# Revit family: Screens-Teknion-JNSEEH_Felt_Elevated_Height_Adjustable_Mounted-R2018
name_source: partatom
category: Furniture
revit_build: Autodesk Revit 2018 (Build: 20190510_1515(x64)
units: mm (PartAtom-declared; Revit-internal decimal feet)

## family parameters
Always vertical = Yes
Cut with Voids When Loaded = No
OmniClass Number = 23.40.20.00
OmniClass Title = General Furniture and Specialties
Room Calculation Point = No
Shared = Yes
Work Plane-Based = No

## types (4) — shared parameters
Assembly Code = E2020200
Manufacturer = Teknion
Manufacturer Fax = 416.661.4586
Part Number = JNSEEH
Product Documentation Link = https://www.teknion.com
Product Line = Expansion Cityline
Product Page URL = https://www.teknion.com
Series = Expansion Cityline
Sustainability Data = https://www.teknion.com
URL = www.teknion.com
Unit Weight URL = http://www.teknion.com
Warranty = http://www.teknion.com

## per-type parameters (varying)
| type | Description | Height | Model | Modesty Base Height |
| 18" from Floor Modesty Base Height, 42" Datum Height | Felt Elevated Screen – Height-Adjustable Table Mounted, 18" Modesty Base Height from Floor, 42" Datum Height, Standard Width, Radius Corner Detail | 42 " | JNSEEH1842__SR | 18.25 " |
| 18" from Floor Modesty Base Height, 51" Datum Height | Felt Elevated Screen – Height-Adjustable Table Mounted, 18" Modesty Base Height from Floor, 51" Datum Height, Standard Width, Radius Corner Detail | 50.83 " | JNSEEH1851__SR | 18.25 " |
| 22" from Floor Modesty Base Height, 42" Datum Height | Felt Elevated Screen – Height-Adjustable Table Mounted, 22" Modesty Base Height from Floor, 42" Datum Height, Standard Width, Radius Corner Detail | 42 " | JNSEEH2242__SR | 22.35 " |
| 22" from Floor Modesty Base Height, 51" Datum Height | Felt Elevated Screen – Height-Adjustable Table Mounted, 22" Modesty Base Height from Floor, 51" Datum Height, Standard Width, Radius Corner Detail | 50.83 " | JNSEEH2251__SR | 22.35 " |

## geometry (parser evidence)
native form markers: Sweep x2
no freeform markers — native parametric forms only
